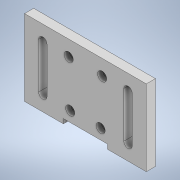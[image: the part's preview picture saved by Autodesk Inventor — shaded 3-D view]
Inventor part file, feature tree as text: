
AUTODESK INVENTOR PART (.ipt)
format: ipt  version: 2020 (Build 240168000, 168)  size: 161,280 bytes
history: native  units: mm
features: sketch x3, extrude x2, hole x1
ambient origin geometry x8: Origin, YZ Plane, XZ Plane, XY Plane, X Axis, Y Axis, Z Axis, Center Point
bodies: Solid1 (feature_tree)
feature tree (6):
  extrude  "Extrusion1"  Depth=50.0mm
  hole  "Hole1"  [1 undecoded]
  extrude  "Extrusion2"  Depth=29.0mm
  sketch  "Sketch1"  dims[d0=80.0mm d1=50.0mm]
  sketch  "Sketch2"  dims[d2=5.5mm d3=12.0mm]
  sketch  "Sketch4"  dims[d5=30.0mm d6=12.0mm d8=5.5mm d9=30.0mm d18=6.0mm d19=0.0mm d28=3.4mm d29=6.0mm d30=6.0mm d31=3.4mm d32=90.0deg d33=8.0mm d34=20.594885mm d38=25.0mm d39=25.0mm d46=29.0mm d47=22.0mm d48=30.0mm d49=20.0mm d50=30.0mm d51=30.0mm d52=10.2mm d53=10.2mm d54=3.0mm d55=25.5mm d56=29.0mm d57=0.0mm d58=0.0mm d35=0.75mm d36=20.594885mm d37=0.0625mm d40=0.375mm d41=14.3117mm d42=0.75mm d43=20.594885mm d44=0.0625mm d45=0.75mm]
note: 1 required parameter value undecoded (feature->parameter linkage not recoverable at this tier; creation-order binding heuristic only, values carry confidence <= 0.55)
